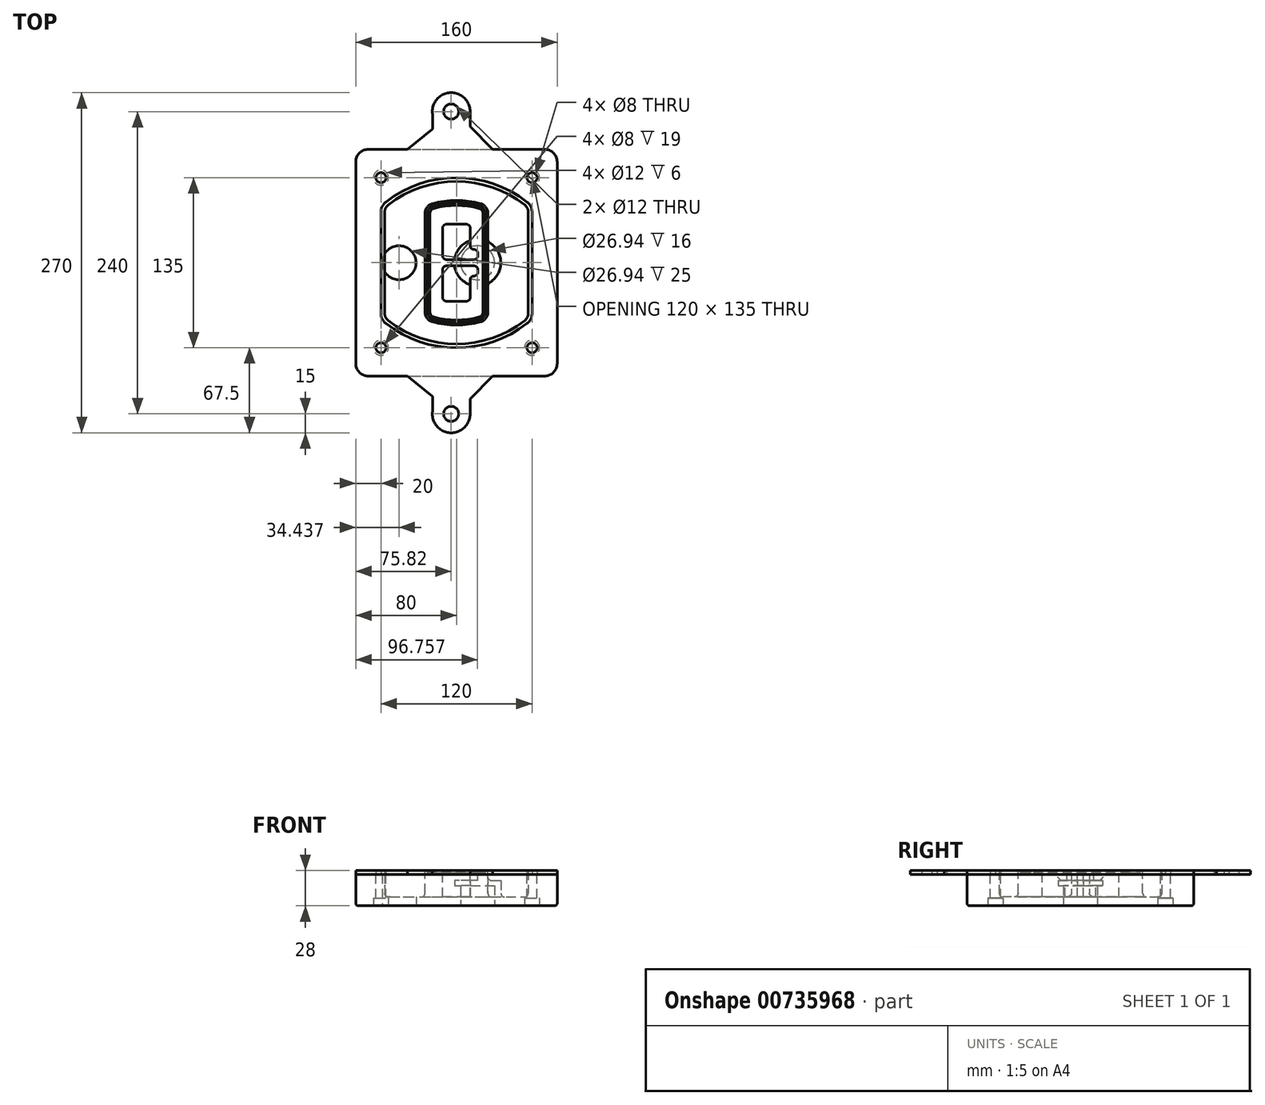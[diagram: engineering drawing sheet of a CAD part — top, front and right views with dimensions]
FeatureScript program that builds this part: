
annotation { "Feature Type Name" : "Feature", "Feature Type Description" : "" }
export const myFeature = defineFeature(function(context is Context, id is Id, definition is map)
    precondition{}
    {
        {
            var Q0;
            Q0=qCreatedBy(makeId("Top.planeOp"),FACE);
            var sketch = newSketch(context, id + "F0", { "sketchPlane" : qUnion([Q0])});
            skPoint(sketch, "E0.rect.middle", {"position": v(0, 0) * mm});
            skLineSegment(sketch, "E1.bottom", {"start": v(-70, -90) * mm, "end": v(70, -90) * mm});
            skLineSegment(sketch, "E1.top", {"start": v(-70, 90) * mm, "end": v(70, 90) * mm});
            skLineSegment(sketch, "E1.left", {"start": v(-80, -80) * mm, "end": v(-80, 80) * mm});
            skLineSegment(sketch, "E1.right", {"start": v(80, -80) * mm, "end": v(80, 80) * mm});
            skLineSegment(sketch, "E2", {"start": v(-80, 90) * mm, "end": v(80, -90) * mm, "construction": true});
            skLineSegment(sketch, "E3", {"start": v(80, 90) * mm, "end": v(-80, -90) * mm, "construction": true});
            skCircle(sketch, "E4", {"center": v(-60, 67.5) * mm, "radius": 4 * mm});
            skCircle(sketch, "E5", {"center": v(60, 67.5) * mm, "radius": 4 * mm});
            skCircle(sketch, "E6", {"center": v(60, -67.5) * mm, "radius": 4 * mm});
            skCircle(sketch, "E7", {"center": v(-60, -67.5) * mm, "radius": 4 * mm});
            skLineSegment(sketch, "E8", {"start": v(-60, 67.5) * mm, "end": v(60, 67.5) * mm, "construction": true});
            skLineSegment(sketch, "E9", {"start": v(60, 67.5) * mm, "end": v(60, -67.5) * mm, "construction": true});
            skLineSegment(sketch, "E10", {"start": v(60, -67.5) * mm, "end": v(-60, -67.5) * mm, "construction": true});
            skLineSegment(sketch, "E11", {"start": v(-60, -67.5) * mm, "end": v(-60, 67.5) * mm, "construction": true});
            skLineSegment(sketch, "E12", {"start": v(-60, 40.3) * mm, "end": v(-60, -40.3) * mm});
            skLineSegment(sketch, "E13", {"start": v(60, 40.3) * mm, "end": v(60, -40.3) * mm});
            skArc(sketch, "E14", {"start": v(56.15, 48.18) * mm, "mid": v(0, 67.5) * mm, "end": v(-56.15, 48.18) * mm});
            skArc(sketch, "E15", {"start": v(-56.15, -48.18) * mm, "mid": v(0, -67.5) * mm, "end": v(56.15, -48.18) * mm});
            skLineSegment(sketch, "E16", {"start": v(-60, 0) * mm, "end": v(60, 0) * mm, "construction": true});
            skPoint(sketch, "E17.visualSharp", {"position": v(-60, -45) * mm});
            skArc(sketch, "E17.filletArc", {"start": v(-60, -40.3) * mm, "mid": v(-58.99, -44.68) * mm, "end": v(-56.15, -48.18) * mm});
            skPoint(sketch, "E18.visualSharp", {"position": v(-60, 45) * mm});
            skArc(sketch, "E18.filletArc", {"start": v(-56.15, 48.18) * mm, "mid": v(-58.99, 44.68) * mm, "end": v(-60, 40.3) * mm});
            skPoint(sketch, "E19.visualSharp", {"position": v(60, 45) * mm});
            skArc(sketch, "E19.filletArc", {"start": v(60, 40.3) * mm, "mid": v(58.99, 44.68) * mm, "end": v(56.15, 48.18) * mm});
            skPoint(sketch, "E20.visualSharp", {"position": v(60, -45) * mm});
            skArc(sketch, "E20.filletArc", {"start": v(56.15, -48.18) * mm, "mid": v(58.99, -44.68) * mm, "end": v(60, -40.3) * mm});
            skPoint(sketch, "E21.visualSharp", {"position": v(-80, 90) * mm});
            skArc(sketch, "E21.filletArc", {"start": v(-70, 90) * mm, "mid": v(-77.07, 87.07) * mm, "end": v(-80, 80) * mm});
            skPoint(sketch, "E22.visualSharp", {"position": v(80, 90) * mm});
            skArc(sketch, "E22.filletArc", {"start": v(80, 80) * mm, "mid": v(77.07, 87.07) * mm, "end": v(70, 90) * mm});
            skPoint(sketch, "E23.visualSharp", {"position": v(80, -90) * mm});
            skArc(sketch, "E23.filletArc", {"start": v(70, -90) * mm, "mid": v(77.07, -87.07) * mm, "end": v(80, -80) * mm});
            skPoint(sketch, "E24.visualSharp", {"position": v(-80, -90) * mm});
            skArc(sketch, "E24.filletArc", {"start": v(-80, -80) * mm, "mid": v(-77.07, -87.07) * mm, "end": v(-70, -90) * mm});
            skArc(sketch, "E25.0", {"start": v(57, 40.3) * mm, "mid": v(56.3, 43.36) * mm, "end": v(54.3, 45.81) * mm});
            skLineSegment(sketch, "E25.1", {"start": v(57, 40.3) * mm, "end": v(57, -40.3) * mm});
            skArc(sketch, "E25.2", {"start": v(54.3, -45.81) * mm, "mid": v(56.3, -43.36) * mm, "end": v(57, -40.3) * mm});
            skArc(sketch, "E25.3", {"start": v(-54.3, -45.81) * mm, "mid": v(0, -64.5) * mm, "end": v(54.3, -45.81) * mm});
            skArc(sketch, "E25.4", {"start": v(-57, -40.3) * mm, "mid": v(-56.3, -43.36) * mm, "end": v(-54.3, -45.81) * mm});
            skArc(sketch, "E25.5", {"start": v(54.3, 45.81) * mm, "mid": v(0, 64.5) * mm, "end": v(-54.3, 45.81) * mm});
            skLineSegment(sketch, "E25.6", {"start": v(-57, 40.3) * mm, "end": v(-57, -40.3) * mm});
            skArc(sketch, "E25.7", {"start": v(-54.3, 45.81) * mm, "mid": v(-56.3, 43.36) * mm, "end": v(-57, 40.3) * mm});
            skArc(sketch, "E26.0", {"start": v(-58.62, 51.33) * mm, "mid": v(-62.58, 46.43) * mm, "end": v(-64, 40.3) * mm});
            skArc(sketch, "E26.1", {"start": v(58.62, 51.33) * mm, "mid": v(0, 71.5) * mm, "end": v(-58.62, 51.33) * mm});
            skArc(sketch, "E26.2", {"start": v(64, 40.3) * mm, "mid": v(62.58, 46.43) * mm, "end": v(58.62, 51.33) * mm});
            skLineSegment(sketch, "E26.3", {"start": v(64, 40.3) * mm, "end": v(64, -40.3) * mm});
            skArc(sketch, "E26.4", {"start": v(58.62, -51.33) * mm, "mid": v(62.58, -46.43) * mm, "end": v(64, -40.3) * mm});
            skLineSegment(sketch, "E26.5", {"start": v(-64, 40.3) * mm, "end": v(-64, -40.3) * mm});
            skArc(sketch, "E26.6", {"start": v(-58.62, -51.33) * mm, "mid": v(0, -71.5) * mm, "end": v(58.62, -51.33) * mm});
            skArc(sketch, "E26.7", {"start": v(-64, -40.3) * mm, "mid": v(-62.58, -46.43) * mm, "end": v(-58.62, -51.33) * mm});
            skSolve(sketch);
        }
        {
            var Q0;
            Q0=makeQuery(id+"F0.imprint","IMPRINT",FACE,{"disambiguationData":[TD([[makeQuery(id+"F0.imprint","IMPRINT",EDGE,{"derivedFrom":sQuery(id+"F0.wireOp",EDGE,"E1.bottom")}),1.0]])]});
            var Q1;
            Q1=makeQuery(id+"F0.imprint","IMPRINT",FACE,{"disambiguationData":[TD([[makeQuery(id+"F0.imprint","IMPRINT",EDGE,{"derivedFrom":sQuery(id+"F0.wireOp",EDGE,"E12")}),1.0]])]});
            var Q2;
            Q2=makeQuery(id+"F0.imprint","IMPRINT",FACE,{"disambiguationData":[TD([[makeQuery(id+"F0.imprint","IMPRINT",EDGE,{"derivedFrom":sQuery(id+"F0.wireOp",EDGE,"E25.0")}),1.0]])]});
            var Q3;
            Q3=makeQuery(id+"F0.imprint","IMPRINT",FACE,{"disambiguationData":[TD([[makeQuery(id+"F0.imprint","IMPRINT",EDGE,{"derivedFrom":sQuery(id+"F0.wireOp",EDGE,"E12")}),-1.0]])]});
            extrude(context, id + "F1", {"entities" : qUnion([Q0, Q1, Q2, Q3]), "oppositeDirection" : true, "depth" : 25 * mm});
        }
        {
            var Q0;
            Q0=makeQuery(id+"F0.imprint","IMPRINT",FACE,{"disambiguationData":[TD([[makeQuery(id+"F0.imprint","IMPRINT",EDGE,{"derivedFrom":sQuery(id+"F0.wireOp",EDGE,"E12")}),1.0]])]});
            extrude(context, id + "F2", {"entities" : qUnion([Q0]), "operationType" : NewBodyOperationType.ADD, "depth" : 3 * mm});
        }
        {
            var Q0;
            Q0=makeQuery(id+"F0.imprint","IMPRINT",FACE,{"disambiguationData":[TD([[makeQuery(id+"F0.imprint","IMPRINT",EDGE,{"derivedFrom":sQuery(id+"F0.wireOp",EDGE,"E25.0")}),1.0]])]});
            extrude(context, id + "F3", {"entities" : qUnion([Q0]), "operationType" : NewBodyOperationType.REMOVE, "oppositeDirection" : true, "depth" : 18 * mm});
        }
        {
            var Q0;
            Q0=makeQuery(id+"F2.opExtrude","CAP_FACE",FACE,{"disambiguationData":[OSD([sQuery(id+"F0.wireOp",EDGE,"E12"),sQuery(id+"F0.wireOp",EDGE,"E13"),sQuery(id+"F0.wireOp",EDGE,"E14"),sQuery(id+"F0.wireOp",EDGE,"E15"),sQuery(id+"F0.wireOp",EDGE,"E17.filletArc"),sQuery(id+"F0.wireOp",EDGE,"E18.filletArc"),sQuery(id+"F0.wireOp",EDGE,"E19.filletArc"),sQuery(id+"F0.wireOp",EDGE,"E20.filletArc"),sQuery(id+"F0.wireOp",EDGE,"E25.0"),sQuery(id+"F0.wireOp",EDGE,"E25.1"),sQuery(id+"F0.wireOp",EDGE,"E25.2"),sQuery(id+"F0.wireOp",EDGE,"E25.3"),sQuery(id+"F0.wireOp",EDGE,"E25.4"),sQuery(id+"F0.wireOp",EDGE,"E25.5"),sQuery(id+"F0.wireOp",EDGE,"E25.6"),sQuery(id+"F0.wireOp",EDGE,"E25.7")])],"isStart":false});
            var sketch = newSketch(context, id + "F4", { "sketchPlane" : qUnion([Q0])});
            skArc(sketch, "E27.0", {"start": v(-19.08, -46.97) * mm, "mid": v(0, -49.5) * mm, "end": v(19.08, -46.97) * mm});
            skArc(sketch, "E28.0", {"start": v(19.08, 46.97) * mm, "mid": v(0, 49.5) * mm, "end": v(-19.08, 46.97) * mm});
            skLineSegment(sketch, "E29", {"start": v(-25, 39.25) * mm, "end": v(-25, -39.25) * mm});
            skLineSegment(sketch, "E30", {"start": v(25, 39.25) * mm, "end": v(25, -39.25) * mm});
            skLineSegment(sketch, "E31", {"start": v(-25, 45.1) * mm, "end": v(25, 45.1) * mm, "construction": true});
            skLineSegment(sketch, "E32", {"start": v(-25, -45.1) * mm, "end": v(25, -45.1) * mm, "construction": true});
            skPoint(sketch, "E33.visualSharp", {"position": v(-25, 45.1) * mm});
            skArc(sketch, "E33.filletArc", {"start": v(-19.08, 46.97) * mm, "mid": v(-23.35, 44.11) * mm, "end": v(-25, 39.25) * mm});
            skPoint(sketch, "E34.visualSharp", {"position": v(25, 45.1) * mm});
            skArc(sketch, "E34.filletArc", {"start": v(25, 39.25) * mm, "mid": v(23.35, 44.11) * mm, "end": v(19.08, 46.97) * mm});
            skPoint(sketch, "E35.visualSharp", {"position": v(25, -45.1) * mm});
            skArc(sketch, "E35.filletArc", {"start": v(19.08, -46.97) * mm, "mid": v(23.35, -44.11) * mm, "end": v(25, -39.25) * mm});
            skPoint(sketch, "E36.visualSharp", {"position": v(-25, -45.1) * mm});
            skArc(sketch, "E36.filletArc", {"start": v(-25, -39.25) * mm, "mid": v(-23.35, -44.11) * mm, "end": v(-19.08, -46.97) * mm});
            skArc(sketch, "E37.0", {"start": v(54.3, 45.81) * mm, "mid": v(0, 64.5) * mm, "end": v(-54.3, 45.81) * mm});
            skArc(sketch, "E37.1", {"start": v(-54.3, 45.81) * mm, "mid": v(-56.3, 43.36) * mm, "end": v(-57, 40.3) * mm});
            skLineSegment(sketch, "E37.2", {"start": v(-57, 40.3) * mm, "end": v(-57, -40.3) * mm});
            skArc(sketch, "E37.3", {"start": v(-57, -40.3) * mm, "mid": v(-56.3, -43.36) * mm, "end": v(-54.3, -45.81) * mm});
            skArc(sketch, "E37.4", {"start": v(-54.3, -45.81) * mm, "mid": v(0, -64.5) * mm, "end": v(54.3, -45.81) * mm});
            skArc(sketch, "E37.5", {"start": v(54.3, -45.81) * mm, "mid": v(56.3, -43.36) * mm, "end": v(57, -40.3) * mm});
            skLineSegment(sketch, "E37.6", {"start": v(57, 40.3) * mm, "end": v(57, -40.3) * mm});
            skArc(sketch, "E37.7", {"start": v(57, 40.3) * mm, "mid": v(56.3, 43.36) * mm, "end": v(54.3, 45.81) * mm});
            skLineSegment(sketch, "E38.0", {"start": v(23, 39.25) * mm, "end": v(23, -39.25) * mm});
            skArc(sketch, "E38.1", {"start": v(18.56, -45.04) * mm, "mid": v(21.76, -42.9) * mm, "end": v(23, -39.25) * mm});
            skArc(sketch, "E38.2", {"start": v(-18.56, -45.04) * mm, "mid": v(0, -47.5) * mm, "end": v(18.56, -45.04) * mm});
            skArc(sketch, "E38.3", {"start": v(-23, -39.25) * mm, "mid": v(-21.76, -42.9) * mm, "end": v(-18.56, -45.04) * mm});
            skLineSegment(sketch, "E38.4", {"start": v(-23, 39.25) * mm, "end": v(-23, -39.25) * mm});
            skArc(sketch, "E38.5", {"start": v(23, 39.25) * mm, "mid": v(21.76, 42.9) * mm, "end": v(18.56, 45.04) * mm});
            skArc(sketch, "E38.6", {"start": v(-18.56, 45.04) * mm, "mid": v(-21.76, 42.9) * mm, "end": v(-23, 39.25) * mm});
            skArc(sketch, "E38.7", {"start": v(18.56, 45.04) * mm, "mid": v(0, 47.5) * mm, "end": v(-18.56, 45.04) * mm});
            skArc(sketch, "E39.0", {"start": v(21, 39.25) * mm, "mid": v(20.18, 41.68) * mm, "end": v(18.04, 43.1) * mm});
            skLineSegment(sketch, "E39.1", {"start": v(21, 39.25) * mm, "end": v(21, -39.25) * mm});
            skArc(sketch, "E39.2", {"start": v(18.04, -43.1) * mm, "mid": v(20.18, -41.68) * mm, "end": v(21, -39.25) * mm});
            skArc(sketch, "E39.3", {"start": v(-18.04, -43.1) * mm, "mid": v(0, -45.5) * mm, "end": v(18.04, -43.1) * mm});
            skArc(sketch, "E39.4", {"start": v(-21, -39.25) * mm, "mid": v(-20.18, -41.68) * mm, "end": v(-18.04, -43.1) * mm});
            skArc(sketch, "E39.5", {"start": v(18.04, 43.1) * mm, "mid": v(0, 45.5) * mm, "end": v(-18.04, 43.1) * mm});
            skLineSegment(sketch, "E39.6", {"start": v(-21, 39.25) * mm, "end": v(-21, -39.25) * mm});
            skArc(sketch, "E39.7", {"start": v(-18.04, 43.1) * mm, "mid": v(-20.18, 41.68) * mm, "end": v(-21, 39.25) * mm});
            skLineSegment(sketch, "E40", {"start": v(-25, 0) * mm, "end": v(25, 0) * mm, "construction": true});
            skLineSegment(sketch, "E41", {"start": v(-11, 5.5) * mm, "end": v(-11, 27.5) * mm});
            skLineSegment(sketch, "E42", {"start": v(-8, 30.5) * mm, "end": v(8, 30.5) * mm});
            skLineSegment(sketch, "E43", {"start": v(11, 27.5) * mm, "end": v(11, 13.5) * mm});
            skLineSegment(sketch, "E44", {"start": v(14, 10.5) * mm, "end": v(14, 10.5) * mm});
            skLineSegment(sketch, "E45", {"start": v(17, 7.5) * mm, "end": v(17, 5.5) * mm});
            skLineSegment(sketch, "E46", {"start": v(14, 2.5) * mm, "end": v(-8, 2.5) * mm});
            skPoint(sketch, "E47.visualSharp", {"position": v(-11, 30.5) * mm});
            skArc(sketch, "E47.filletArc", {"start": v(-8, 30.5) * mm, "mid": v(-10.12, 29.62) * mm, "end": v(-11, 27.5) * mm});
            skPoint(sketch, "E48.visualSharp", {"position": v(11, 30.5) * mm});
            skArc(sketch, "E48.filletArc", {"start": v(11, 27.5) * mm, "mid": v(10.12, 29.62) * mm, "end": v(8, 30.5) * mm});
            skPoint(sketch, "E49.visualSharp", {"position": v(11, 10.5) * mm});
            skArc(sketch, "E49.filletArc", {"start": v(11, 13.5) * mm, "mid": v(11.88, 11.38) * mm, "end": v(14, 10.5) * mm});
            skPoint(sketch, "E50.visualSharp", {"position": v(17, 10.5) * mm});
            skArc(sketch, "E50.filletArc", {"start": v(17, 7.5) * mm, "mid": v(16.12, 9.62) * mm, "end": v(14, 10.5) * mm});
            skPoint(sketch, "E51.visualSharp", {"position": v(17, 2.5) * mm});
            skArc(sketch, "E51.filletArc", {"start": v(14, 2.5) * mm, "mid": v(16.12, 3.38) * mm, "end": v(17, 5.5) * mm});
            skPoint(sketch, "E52.visualSharp", {"position": v(-11, 2.5) * mm});
            skArc(sketch, "E52.filletArc", {"start": v(-11, 5.5) * mm, "mid": v(-10.12, 3.38) * mm, "end": v(-8, 2.5) * mm});
            skLineSegment(sketch, "E53.0.MirrorCS", {"start": v(14, -2.5) * mm, "end": v(-8, -2.5) * mm});
            skArc(sketch, "E54.0.MirrorCS", {"start": v(-11, -5.5) * mm, "mid": v(-10.12, -3.38) * mm, "end": v(-8, -2.5) * mm});
            skLineSegment(sketch, "E55.0.MirrorCS", {"start": v(-11, -5.5) * mm, "end": v(-11, -27.5) * mm});
            skArc(sketch, "E56.0.MirrorCS", {"start": v(-8, -30.5) * mm, "mid": v(-10.12, -29.62) * mm, "end": v(-11, -27.5) * mm});
            skLineSegment(sketch, "E57.0.MirrorCS", {"start": v(-8, -30.5) * mm, "end": v(8, -30.5) * mm});
            skArc(sketch, "E58.0.MirrorCS", {"start": v(11, -27.5) * mm, "mid": v(10.12, -29.62) * mm, "end": v(8, -30.5) * mm});
            skLineSegment(sketch, "E59.0.MirrorCS", {"start": v(11, -27.5) * mm, "end": v(11, -13.5) * mm});
            skArc(sketch, "E60.0.MirrorCS", {"start": v(11, -13.5) * mm, "mid": v(11.88, -11.38) * mm, "end": v(14, -10.5) * mm});
            skArc(sketch, "E61.0.MirrorCS", {"start": v(17, -7.5) * mm, "mid": v(16.12, -9.62) * mm, "end": v(14, -10.5) * mm});
            skLineSegment(sketch, "E62.0.MirrorCS", {"start": v(17, -7.5) * mm, "end": v(17, -5.5) * mm});
            skArc(sketch, "E63.0.MirrorCS", {"start": v(14, -2.5) * mm, "mid": v(16.12, -3.38) * mm, "end": v(17, -5.5) * mm});
            skSolve(sketch);
        }
        {
            var Q0;
            Q0=makeQuery(id+"F4.imprint","IMPRINT",FACE,{"disambiguationData":[TD([[makeQuery(id+"F4.imprint","IMPRINT",EDGE,{"derivedFrom":sQuery(id+"F4.wireOp",EDGE,"E27.0")}),1.0]])]});
            var Q1;
            Q1=makeQuery(id+"F4.imprint","IMPRINT",FACE,{"disambiguationData":[TD([[makeQuery(id+"F4.imprint","IMPRINT",EDGE,{"derivedFrom":sQuery(id+"F4.wireOp",EDGE,"E38.0")}),-1.0]])]});
            var Q2;
            Q2=makeQuery(id+"F4.imprint","IMPRINT",FACE,{"disambiguationData":[TD([[makeQuery(id+"F4.imprint","IMPRINT",EDGE,{"derivedFrom":sQuery(id+"F4.wireOp",EDGE,"E39.0")}),1.0]])]});
            extrude(context, id + "F5", {"entities" : qUnion([Q0, Q1, Q2]), "operationType" : NewBodyOperationType.ADD, "endBound" : BoundingType.UP_TO_NEXT, "oppositeDirection" : true, "depth" : 25 * mm});
        }
        {
            var Q0;
            Q0=makeQuery(id+"F4.imprint","IMPRINT",FACE,{"disambiguationData":[TD([[makeQuery(id+"F4.imprint","IMPRINT",EDGE,{"derivedFrom":sQuery(id+"F4.wireOp",EDGE,"E38.0")}),-1.0]])]});
            extrude(context, id + "F6", {"entities" : qUnion([Q0]), "operationType" : NewBodyOperationType.REMOVE, "oppositeDirection" : true, "depth" : 2 * mm});
        }
        {
            var Q0;
            Q0=makeQuery(id+"F1.opExtrude","CAP_FACE",FACE,{"disambiguationData":[OSD([sQuery(id+"F0.wireOp",EDGE,"E1.bottom"),sQuery(id+"F0.wireOp",EDGE,"E1.top"),sQuery(id+"F0.wireOp",EDGE,"E1.left"),sQuery(id+"F0.wireOp",EDGE,"E1.right"),sQuery(id+"F0.wireOp",EDGE,"E4"),sQuery(id+"F0.wireOp",EDGE,"E5"),sQuery(id+"F0.wireOp",EDGE,"E6"),sQuery(id+"F0.wireOp",EDGE,"E7"),sQuery(id+"F0.wireOp",EDGE,"E21.filletArc"),sQuery(id+"F0.wireOp",EDGE,"E22.filletArc"),sQuery(id+"F0.wireOp",EDGE,"E23.filletArc"),sQuery(id+"F0.wireOp",EDGE,"E24.filletArc")])],"isStart":false});
            var sketch = newSketch(context, id + "F7", { "sketchPlane" : qUnion([Q0])});
            skCircle(sketch, "E64", {"center": v(16.76, 0) * mm, "radius": 13.47 * mm});
            skCircle(sketch, "E65", {"center": v(-45.56, 0) * mm, "radius": 13.47 * mm});
            skLineSegment(sketch, "E66", {"start": v(80, 0) * mm, "end": v(-80, 0) * mm});
            skCircle(sketch, "E67", {"center": v(16.76, 0) * mm, "radius": 18.47 * mm});
            skCircle(sketch, "E68", {"center": v(60, -67.5) * mm, "radius": 6 * mm});
            skCircle(sketch, "E69", {"center": v(-60, -67.5) * mm, "radius": 6 * mm});
            skCircle(sketch, "E70", {"center": v(-60, 67.5) * mm, "radius": 6 * mm});
            skCircle(sketch, "E71", {"center": v(60, 67.5) * mm, "radius": 6 * mm});
            skSolve(sketch);
        }
        {
            var Q0;
            {var subQ1=sQuery(id+"F7.wireOp",EDGE,"E66");var subQ4=sQuery(id+"F7.wireOp",EDGE,"E64");var subQ6=makeQuery(id+"F7.imprint","INTERSECT",VERTEX,{"disambiguationData":[OD(0.0)],"derivedFrom":[subQ4,subQ1]});Q0=makeQuery(id+"F7.imprint","IMPRINT",FACE,{"disambiguationData":[TD([[makeQuery(id+"F7.imprint","IMPRINT",EDGE,{"disambiguationData":[TD([[subQ6,-1.0]])],"derivedFrom":subQ4}),-1.0]])]});}
            var Q1;
            {var subQ0=sQuery(id+"F7.wireOp",EDGE,"E66");var subQ1=sQuery(id+"F7.wireOp",EDGE,"E64");var subQ3=makeQuery(id+"F7.imprint","INTERSECT",VERTEX,{"disambiguationData":[OD(0.0)],"derivedFrom":[subQ1,subQ0]});Q1=makeQuery(id+"F7.imprint","IMPRINT",FACE,{"disambiguationData":[TD([[makeQuery(id+"F7.imprint","IMPRINT",EDGE,{"disambiguationData":[TD([[subQ3,-1.0]])],"derivedFrom":subQ1}),1.0]])]});}
            var Q2;
            {var subQ0=sQuery(id+"F7.wireOp",EDGE,"E66");var subQ1=sQuery(id+"F7.wireOp",EDGE,"E64");var subQ3=makeQuery(id+"F7.imprint","INTERSECT",VERTEX,{"disambiguationData":[OD(0.0)],"derivedFrom":[subQ1,subQ0]});Q2=makeQuery(id+"F7.imprint","IMPRINT",FACE,{"disambiguationData":[TD([[makeQuery(id+"F7.imprint","IMPRINT",EDGE,{"disambiguationData":[TD([[subQ3,1.0]])],"derivedFrom":subQ1}),1.0]])]});}
            var Q3;
            {var subQ1=sQuery(id+"F7.wireOp",EDGE,"E66");var subQ4=sQuery(id+"F7.wireOp",EDGE,"E64");var subQ6=makeQuery(id+"F7.imprint","INTERSECT",VERTEX,{"disambiguationData":[OD(0.0)],"derivedFrom":[subQ4,subQ1]});Q3=makeQuery(id+"F7.imprint","IMPRINT",FACE,{"disambiguationData":[TD([[makeQuery(id+"F7.imprint","IMPRINT",EDGE,{"disambiguationData":[TD([[subQ6,1.0]])],"derivedFrom":subQ4}),-1.0]])]});}
            extrude(context, id + "F8", {"entities" : qUnion([Q0, Q1, Q2, Q3]), "operationType" : NewBodyOperationType.ADD, "oppositeDirection" : true, "depth" : 20 * mm});
        }
        {
            var Q0;
            {var subQ0=sQuery(id+"F7.wireOp",EDGE,"E66");var subQ1=sQuery(id+"F7.wireOp",EDGE,"E64");var subQ3=makeQuery(id+"F7.imprint","INTERSECT",VERTEX,{"disambiguationData":[OD(0.0)],"derivedFrom":[subQ1,subQ0]});Q0=makeQuery(id+"F7.imprint","IMPRINT",FACE,{"disambiguationData":[TD([[makeQuery(id+"F7.imprint","IMPRINT",EDGE,{"disambiguationData":[TD([[subQ3,-1.0]])],"derivedFrom":subQ1}),1.0]])]});}
            var Q1;
            {var subQ0=sQuery(id+"F7.wireOp",EDGE,"E66");var subQ1=sQuery(id+"F7.wireOp",EDGE,"E64");var subQ3=makeQuery(id+"F7.imprint","INTERSECT",VERTEX,{"disambiguationData":[OD(0.0)],"derivedFrom":[subQ1,subQ0]});Q1=makeQuery(id+"F7.imprint","IMPRINT",FACE,{"disambiguationData":[TD([[makeQuery(id+"F7.imprint","IMPRINT",EDGE,{"disambiguationData":[TD([[subQ3,1.0]])],"derivedFrom":subQ1}),1.0]])]});}
            extrude(context, id + "F9", {"entities" : qUnion([Q0, Q1]), "operationType" : NewBodyOperationType.REMOVE, "oppositeDirection" : true, "depth" : 16 * mm});
        }
        {
            var Q0;
            {var subQ0=sQuery(id+"F7.wireOp",EDGE,"E66");var subQ1=sQuery(id+"F7.wireOp",EDGE,"E65");var subQ3=makeQuery(id+"F7.imprint","INTERSECT",VERTEX,{"disambiguationData":[OD(0.0)],"derivedFrom":[subQ1,subQ0]});Q0=makeQuery(id+"F7.imprint","IMPRINT",FACE,{"disambiguationData":[TD([[makeQuery(id+"F7.imprint","IMPRINT",EDGE,{"disambiguationData":[TD([[subQ3,-1.0]])],"derivedFrom":subQ1}),1.0]])]});}
            var Q1;
            {var subQ0=sQuery(id+"F7.wireOp",EDGE,"E66");var subQ1=sQuery(id+"F7.wireOp",EDGE,"E65");var subQ3=makeQuery(id+"F7.imprint","INTERSECT",VERTEX,{"disambiguationData":[OD(0.0)],"derivedFrom":[subQ1,subQ0]});Q1=makeQuery(id+"F7.imprint","IMPRINT",FACE,{"disambiguationData":[TD([[makeQuery(id+"F7.imprint","IMPRINT",EDGE,{"disambiguationData":[TD([[subQ3,1.0]])],"derivedFrom":subQ1}),1.0]])]});}
            extrude(context, id + "F10", {"entities" : qUnion([Q0, Q1]), "operationType" : NewBodyOperationType.REMOVE, "oppositeDirection" : true, "depth" : 25 * mm});
        }
        {
            var Q0;
            Q0=makeQuery(id+"F7.imprint","IMPRINT",FACE,{"disambiguationData":[TD([[makeQuery(id+"F7.imprint","IMPRINT",EDGE,{"derivedFrom":sQuery(id+"F7.wireOp",EDGE,"E68")}),1.0]])]});
            var Q1;
            Q1=makeQuery(id+"F7.imprint","IMPRINT",FACE,{"disambiguationData":[TD([[makeQuery(id+"F7.imprint","IMPRINT",EDGE,{"derivedFrom":makeQuery(id+"F1.opExtrude","CAP_EDGE",EDGE,{"disambiguationData":[OSD([sQuery(id+"F0.wireOp",EDGE,"E5")])],"isStart":false})}),-1.0]])]});
            var Q2;
            Q2=makeQuery(id+"F7.imprint","IMPRINT",FACE,{"disambiguationData":[TD([[makeQuery(id+"F7.imprint","IMPRINT",EDGE,{"derivedFrom":sQuery(id+"F7.wireOp",EDGE,"E69")}),1.0]])]});
            var Q3;
            Q3=makeQuery(id+"F7.imprint","IMPRINT",FACE,{"disambiguationData":[TD([[makeQuery(id+"F7.imprint","IMPRINT",EDGE,{"derivedFrom":makeQuery(id+"F1.opExtrude","CAP_EDGE",EDGE,{"disambiguationData":[OSD([sQuery(id+"F0.wireOp",EDGE,"E4")])],"isStart":false})}),-1.0]])]});
            var Q4;
            Q4=makeQuery(id+"F7.imprint","IMPRINT",FACE,{"disambiguationData":[TD([[makeQuery(id+"F7.imprint","IMPRINT",EDGE,{"derivedFrom":sQuery(id+"F7.wireOp",EDGE,"E70")}),1.0]])]});
            var Q5;
            Q5=makeQuery(id+"F7.imprint","IMPRINT",FACE,{"disambiguationData":[TD([[makeQuery(id+"F7.imprint","IMPRINT",EDGE,{"derivedFrom":makeQuery(id+"F1.opExtrude","CAP_EDGE",EDGE,{"disambiguationData":[OSD([sQuery(id+"F0.wireOp",EDGE,"E7")])],"isStart":false})}),-1.0]])]});
            var Q6;
            Q6=makeQuery(id+"F7.imprint","IMPRINT",FACE,{"disambiguationData":[TD([[makeQuery(id+"F7.imprint","IMPRINT",EDGE,{"derivedFrom":sQuery(id+"F7.wireOp",EDGE,"E71")}),1.0]])]});
            var Q7;
            Q7=makeQuery(id+"F7.imprint","IMPRINT",FACE,{"disambiguationData":[TD([[makeQuery(id+"F7.imprint","IMPRINT",EDGE,{"derivedFrom":makeQuery(id+"F1.opExtrude","CAP_EDGE",EDGE,{"disambiguationData":[OSD([sQuery(id+"F0.wireOp",EDGE,"E6")])],"isStart":false})}),-1.0]])]});
            extrude(context, id + "F11", {"entities" : qUnion([Q0, Q1, Q2, Q3, Q4, Q5, Q6, Q7]), "operationType" : NewBodyOperationType.REMOVE, "oppositeDirection" : true, "depth" : 6 * mm});
        }
        {
            var Q0;
            Q0=makeQuery(id+"F9.boolean.opBoolean","COPY",FACE,{"derivedFrom":makeQuery(id+"F9.opExtrude","CAP_FACE",FACE,{"disambiguationData":[OSD([sQuery(id+"F7.wireOp",EDGE,"E64")])],"isStart":false})});
            var sketch = newSketch(context, id + "F12", { "sketchPlane" : qUnion([Q0])});
            skArc(sketch, "E72.0", {"start": v(11, 17.55) * mm, "mid": v(2.57, 11.82) * mm, "end": v(-1.54, 2.5) * mm});
            skArc(sketch, "E72.1", {"start": v(-1.54, -2.5) * mm, "mid": v(2.57, -11.82) * mm, "end": v(11, -17.55) * mm});
            skLineSegment(sketch, "E73", {"start": v(-1.54, -2.5) * mm, "end": v(14, -2.5) * mm});
            skLineSegment(sketch, "E74.0", {"start": v(14, 2.5) * mm, "end": v(-1.54, 2.5) * mm});
            skArc(sketch, "E74.1", {"start": v(14, 2.5) * mm, "mid": v(16.12, 3.38) * mm, "end": v(17, 5.5) * mm});
            skLineSegment(sketch, "E74.2", {"start": v(17, 7.5) * mm, "end": v(17, 5.5) * mm});
            skArc(sketch, "E74.3", {"start": v(17, 7.5) * mm, "mid": v(16.12, 9.62) * mm, "end": v(14, 10.5) * mm});
            skArc(sketch, "E74.4", {"start": v(11, 13.5) * mm, "mid": v(11.88, 11.38) * mm, "end": v(14, 10.5) * mm});
            skLineSegment(sketch, "E74.5", {"start": v(11, 17.55) * mm, "end": v(11, 13.5) * mm});
            skLineSegment(sketch, "E74.7", {"start": v(14, -2.5) * mm, "end": v(-1.54, -2.5) * mm});
            skArc(sketch, "E74.8", {"start": v(14, -2.5) * mm, "mid": v(16.12, -3.38) * mm, "end": v(17, -5.5) * mm});
            skLineSegment(sketch, "E74.9", {"start": v(17, -7.5) * mm, "end": v(17, -5.5) * mm});
            skArc(sketch, "E74.10", {"start": v(17, -7.5) * mm, "mid": v(16.12, -9.62) * mm, "end": v(14, -10.5) * mm});
            skArc(sketch, "E74.11", {"start": v(11, -13.5) * mm, "mid": v(11.88, -11.38) * mm, "end": v(14, -10.5) * mm});
            skLineSegment(sketch, "E74.12", {"start": v(11, -17.55) * mm, "end": v(11, -13.5) * mm});
            skPoint(sketch, "E75.orphan", {"position": v(11, -27.5) * mm});
            skPoint(sketch, "E76.orphan", {"position": v(-8, -2.5) * mm});
            skPoint(sketch, "E77.orphan", {"position": v(-8, 2.5) * mm});
            skPoint(sketch, "E78.orphan", {"position": v(11, 27.5) * mm});
            skSolve(sketch);
        }
        {
            var Q0;
            {var subQ7=sQuery(id+"F12.wireOp",EDGE,"E72.0");var subQ14=sQuery(id+"F12.wireOp",EDGE,"E72.1");var subQ16=sQuery(id+"F12.wireOp",EDGE,"E74.1");var subQ18=sQuery(id+"F12.wireOp",EDGE,"E74.8");Q0=qUnion([makeQuery(id+"F12.imprint","IMPRINT",FACE,{"disambiguationData":[TD([[makeQuery(id+"F12.imprint","IMPRINT",EDGE,{"derivedFrom":subQ7}),1.0]])]}),makeQuery(id+"F12.imprint","IMPRINT",FACE,{"disambiguationData":[TD([[makeQuery(id+"F12.imprint","IMPRINT",EDGE,{"derivedFrom":subQ14}),1.0]])]}),makeQuery(id+"F12.imprint","IMPRINT",FACE,{"disambiguationData":[TD([[makeQuery(id+"F12.imprint","IMPRINT",EDGE,{"derivedFrom":subQ16}),1.0]])]}),makeQuery(id+"F12.imprint","IMPRINT",FACE,{"disambiguationData":[TD([[makeQuery(id+"F12.imprint","IMPRINT",EDGE,{"derivedFrom":subQ18}),-1.0]])]})]);}
            var Q1;
            Q1=makeQuery(id+"F5.boolean.opBoolean","SPLIT",FACE,{"disambiguationData":[TD([makeQuery(id+"F5.opExtrude","SWEPT_FACE",FACE,{"disambiguationData":[OSD([sQuery(id+"F4.wireOp",EDGE,"E41")])]})])],"derivedFrom":makeQuery(id+"F3.boolean.opBoolean","COPY",FACE,{"derivedFrom":makeQuery(id+"F3.opExtrude","CAP_FACE",FACE,{"disambiguationData":[OSD([sQuery(id+"F0.wireOp",EDGE,"E25.0"),sQuery(id+"F0.wireOp",EDGE,"E25.1"),sQuery(id+"F0.wireOp",EDGE,"E25.2"),sQuery(id+"F0.wireOp",EDGE,"E25.3"),sQuery(id+"F0.wireOp",EDGE,"E25.4"),sQuery(id+"F0.wireOp",EDGE,"E25.5"),sQuery(id+"F0.wireOp",EDGE,"E25.6"),sQuery(id+"F0.wireOp",EDGE,"E25.7")])],"isStart":false})})});
            extrude(context, id + "F13", {"entities" : qUnion([Q0]), "operationType" : NewBodyOperationType.REMOVE, "endBound" : BoundingType.UP_TO_SURFACE, "endBoundEntityFace" : qUnion([Q1]), "depth" : 25 * mm});
        }
        {
            var Q0;
            Q0=makeQuery(id+"F3.boolean.opBoolean","COPY",EDGE,{"derivedFrom":makeQuery(id+"F3.opExtrude","CAP_EDGE",EDGE,{"disambiguationData":[OSD([sQuery(id+"F0.wireOp",EDGE,"E25.6")])],"isStart":false})});
            var Q1;
            Q1=makeQuery(id+"F8.boolean.opBoolean","INTERSECT",EDGE,{"derivedFrom":[makeQuery(id+"F5.opExtrude","SWEPT_FACE",FACE,{"disambiguationData":[OSD([sQuery(id+"F4.wireOp",EDGE,"E30")])]}),makeQuery(id+"F8.opExtrude","CAP_FACE",FACE,{"disambiguationData":[OSD([sQuery(id+"F7.wireOp",EDGE,"E67")])],"isStart":false})]});
            var Q2;
            Q2=makeQuery(id+"F8.boolean.opBoolean","INTERSECT",EDGE,{"disambiguationData":[OD(1.0)],"derivedFrom":[makeQuery(id+"F5.opExtrude","SWEPT_FACE",FACE,{"disambiguationData":[OSD([sQuery(id+"F4.wireOp",EDGE,"E30")])]}),makeQuery(id+"F8.opExtrude","SWEPT_FACE",FACE,{"disambiguationData":[OSD([sQuery(id+"F7.wireOp",EDGE,"E67")])]})]});
            var Q3;
            {var subQ0=sQuery(id+"F4.wireOp",EDGE,"E30");Q3=makeQuery(id+"F8.boolean.opBoolean","SPLIT",EDGE,{"disambiguationData":[TD([makeQuery(id+"F5.opExtrude","SWEPT_FACE",FACE,{"disambiguationData":[OSD([sQuery(id+"F4.wireOp",EDGE,"E35.filletArc")])]})])],"derivedFrom":makeQuery(id+"F5.opExtrude","CAP_EDGE",EDGE,{"disambiguationData":[OSD([subQ0])],"isStart":false})});}
            var Q4;
            {var subQ0=sQuery(id+"F0.wireOp",EDGE,"E25.7");var subQ1=sQuery(id+"F0.wireOp",EDGE,"E25.1");var subQ2=sQuery(id+"F0.wireOp",EDGE,"E25.6");var subQ3=sQuery(id+"F0.wireOp",EDGE,"E25.5");var subQ4=sQuery(id+"F0.wireOp",EDGE,"E25.4");var subQ5=sQuery(id+"F0.wireOp",EDGE,"E25.0");var subQ6=sQuery(id+"F0.wireOp",EDGE,"E25.2");var subQ7=sQuery(id+"F0.wireOp",EDGE,"E25.3");Q4=makeQuery(id+"F8.boolean.opBoolean","INTERSECT",EDGE,{"derivedFrom":[makeQuery(id+"F5.boolean.opBoolean","SPLIT",FACE,{"disambiguationData":[TD([makeQuery(id+"F2.opExtrude","SWEPT_FACE",FACE,{"disambiguationData":[OSD([subQ5])]})])],"derivedFrom":makeQuery(id+"F3.boolean.opBoolean","COPY",FACE,{"derivedFrom":makeQuery(id+"F3.opExtrude","CAP_FACE",FACE,{"disambiguationData":[OSD([subQ5,subQ1,subQ6,subQ7,subQ4,subQ3,subQ2,subQ0])],"isStart":false})})}),makeQuery(id+"F8.opExtrude","SWEPT_FACE",FACE,{"disambiguationData":[OSD([sQuery(id+"F7.wireOp",EDGE,"E67")])]})]});}
            var Q5;
            Q5=makeQuery(id+"F8.boolean.opBoolean","INTERSECT",EDGE,{"disambiguationData":[OD(0.0)],"derivedFrom":[makeQuery(id+"F5.opExtrude","SWEPT_FACE",FACE,{"disambiguationData":[OSD([sQuery(id+"F4.wireOp",EDGE,"E30")])]}),makeQuery(id+"F8.opExtrude","SWEPT_FACE",FACE,{"disambiguationData":[OSD([sQuery(id+"F7.wireOp",EDGE,"E67")])]})]});
            fillet(context, id + "F14", {"entities" : qUnion([Q0, Q1, Q2, Q3, Q4, Q5]), "radius" : 3 * mm, "tangentPropagation" : true, "allowEdgeOverflow" : false});
        }
        {
            var Q0;
            Q0=makeQuery(id+"F1.opExtrude","CAP_EDGE",EDGE,{"disambiguationData":[OSD([sQuery(id+"F0.wireOp",EDGE,"E1.bottom")])],"isStart":false});
            fillet(context, id + "F15", {"entities" : qUnion([Q0]), "radius" : 2 * mm, "tangentPropagation" : true, "allowEdgeOverflow" : false});
        }
        {
            var Q0;
            {var subQ0=sQuery(id+"F0.wireOp",EDGE,"E21.filletArc");var subQ1=sQuery(id+"F0.wireOp",EDGE,"E7");var subQ2=sQuery(id+"F0.wireOp",EDGE,"E6");var subQ3=sQuery(id+"F0.wireOp",EDGE,"E5");var subQ4=sQuery(id+"F0.wireOp",EDGE,"E4");var subQ5=sQuery(id+"F0.wireOp",EDGE,"E22.filletArc");var subQ6=sQuery(id+"F0.wireOp",EDGE,"E1.bottom");var subQ7=sQuery(id+"F0.wireOp",EDGE,"E1.right");var subQ8=sQuery(id+"F0.wireOp",EDGE,"E1.top");var subQ9=sQuery(id+"F0.wireOp",EDGE,"E1.left");var subQ10=sQuery(id+"F0.wireOp",EDGE,"E23.filletArc");var subQ11=sQuery(id+"F0.wireOp",EDGE,"E24.filletArc");Q0=makeQuery(id+"F2.boolean.opBoolean","SPLIT",FACE,{"disambiguationData":[TD([makeQuery(id+"F1.opExtrude","SWEPT_FACE",FACE,{"disambiguationData":[OSD([subQ6])]})])],"derivedFrom":makeQuery(id+"F1.opExtrude","CAP_FACE",FACE,{"disambiguationData":[OSD([subQ6,subQ8,subQ9,subQ7,subQ4,subQ3,subQ2,subQ1,subQ0,subQ5,subQ10,subQ11])],"isStart":true})});}
            var sketch = newSketch(context, id + "F16", { "sketchPlane" : qUnion([Q0])});
            skLineSegment(sketch, "E79", {"start": v(-38.8, 90) * mm, "end": v(-19.06, 106.08) * mm});
            skLineSegment(sketch, "E80", {"start": v(-19.06, 106.08) * mm, "end": v(-19.06, 118.08) * mm});
            skLineSegment(sketch, "E81", {"start": v(10.82, 120) * mm, "end": v(10.82, 108) * mm});
            skLineSegment(sketch, "E82", {"start": v(10.82, 108) * mm, "end": v(28.82, 90) * mm});
            skArc(sketch, "E83", {"start": v(10.82, 120) * mm, "mid": v(-5.14, 134.97) * mm, "end": v(-19.06, 118.08) * mm});
            skCircle(sketch, "E84", {"center": v(-4.18, 120) * mm, "radius": 6 * mm});
            skLineSegment(sketch, "E85", {"start": v(-38.8, 90) * mm, "end": v(28.82, 90) * mm});
            skLineSegment(sketch, "E86.MirrorCS", {"start": v(-38.8, -90) * mm, "end": v(-19.06, -106.08) * mm});
            skLineSegment(sketch, "E87.MirrorCS", {"start": v(-19.06, -106.08) * mm, "end": v(-19.06, -118.08) * mm});
            skArc(sketch, "E88.MirrorCS", {"start": v(10.82, -120) * mm, "mid": v(-5.14, -134.97) * mm, "end": v(-19.06, -118.08) * mm});
            skCircle(sketch, "E89.MirrorC", {"center": v(-4.18, -120) * mm, "radius": 6 * mm});
            skLineSegment(sketch, "E90.MirrorCS", {"start": v(10.82, -120) * mm, "end": v(10.82, -108) * mm});
            skLineSegment(sketch, "E91.MirrorCS", {"start": v(10.82, -108) * mm, "end": v(28.82, -90) * mm});
            skPoint(sketch, "E92.end.orphan", {"position": v(80, 0) * mm});
            skPoint(sketch, "E92.start.orphan", {"position": v(-80, 0) * mm});
            skSolve(sketch);
        }
        {
            var Q0;
            {var subQ5=sQuery(id+"F16.wireOp",EDGE,"E85");Q0=makeQuery(id+"F16.imprint","IMPRINT",FACE,{"disambiguationData":[TD([[makeQuery(id+"F16.imprint","IMPRINT",EDGE,{"derivedFrom":subQ5}),-1.0]])]});}
            var Q1;
            Q1=makeQuery(id+"F16.imprint","IMPRINT",FACE,{"disambiguationData":[TD([[makeQuery(id+"F16.imprint","IMPRINT",EDGE,{"derivedFrom":sQuery(id+"F16.wireOp",EDGE,"E79")}),-1.0]])]});
            var Q2;
            {var subQ0=sQuery(id+"F16.wireOp",EDGE,"E86.MirrorCS");Q2=makeQuery(id+"F16.imprint","IMPRINT",FACE,{"disambiguationData":[TD([[makeQuery(id+"F16.imprint","IMPRINT",EDGE,{"derivedFrom":subQ0}),1.0]])]});}
            var Q3;
            Q3=makeQuery(id+"F2.opExtrude","CAP_FACE",FACE,{"disambiguationData":[OSD([sQuery(id+"F0.wireOp",EDGE,"E12"),sQuery(id+"F0.wireOp",EDGE,"E13"),sQuery(id+"F0.wireOp",EDGE,"E14"),sQuery(id+"F0.wireOp",EDGE,"E15"),sQuery(id+"F0.wireOp",EDGE,"E17.filletArc"),sQuery(id+"F0.wireOp",EDGE,"E18.filletArc"),sQuery(id+"F0.wireOp",EDGE,"E19.filletArc"),sQuery(id+"F0.wireOp",EDGE,"E20.filletArc"),sQuery(id+"F0.wireOp",EDGE,"E25.0"),sQuery(id+"F0.wireOp",EDGE,"E25.1"),sQuery(id+"F0.wireOp",EDGE,"E25.2"),sQuery(id+"F0.wireOp",EDGE,"E25.3"),sQuery(id+"F0.wireOp",EDGE,"E25.4"),sQuery(id+"F0.wireOp",EDGE,"E25.5"),sQuery(id+"F0.wireOp",EDGE,"E25.6"),sQuery(id+"F0.wireOp",EDGE,"E25.7")])],"isStart":false});
            extrude(context, id + "F17", {"entities" : qUnion([Q0, Q1, Q2]), "depth" : 3 * mm, "endBoundEntityFace" : qUnion([Q3]), "offsetDistance" : 25 * mm});
        }
    });
